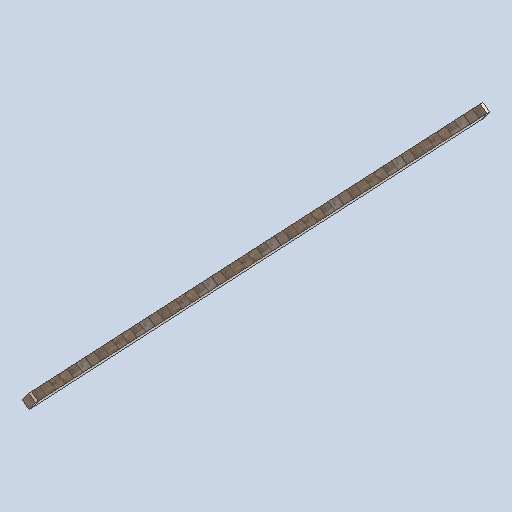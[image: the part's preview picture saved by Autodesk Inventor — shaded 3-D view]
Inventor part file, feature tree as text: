
AUTODESK INVENTOR PART (.ipt)
format: ipt  version: 2024.2 (Build 282272000, 272)  size: 131,584 bytes
history: native  units: in
note: dims shown in document units (in); Inventor stores cm internally (conversion verified against a paired STEP export)
features: sketch x4, other x3, plane x2
ambient origin geometry x8: Origin, YZ Plane, XZ Plane, XY Plane, X Axis, Y Axis, Z Axis, Center Point
bodies: Solid1 (feature_tree)
feature tree (9):
  other  "support_beam_segment_0104.ipt"
  other  "Solid1::support_beam_segment_0104.ipt"
  other  "TaggingFeature1"
  sketch  "Sketch1"  dims[d0=0.3937in]
  sketch  "Sketch2"
  sketch  "Sketch3"
  sketch  "Sketch4"
  plane  "Work Plane1"
  plane  "Work Plane2"
